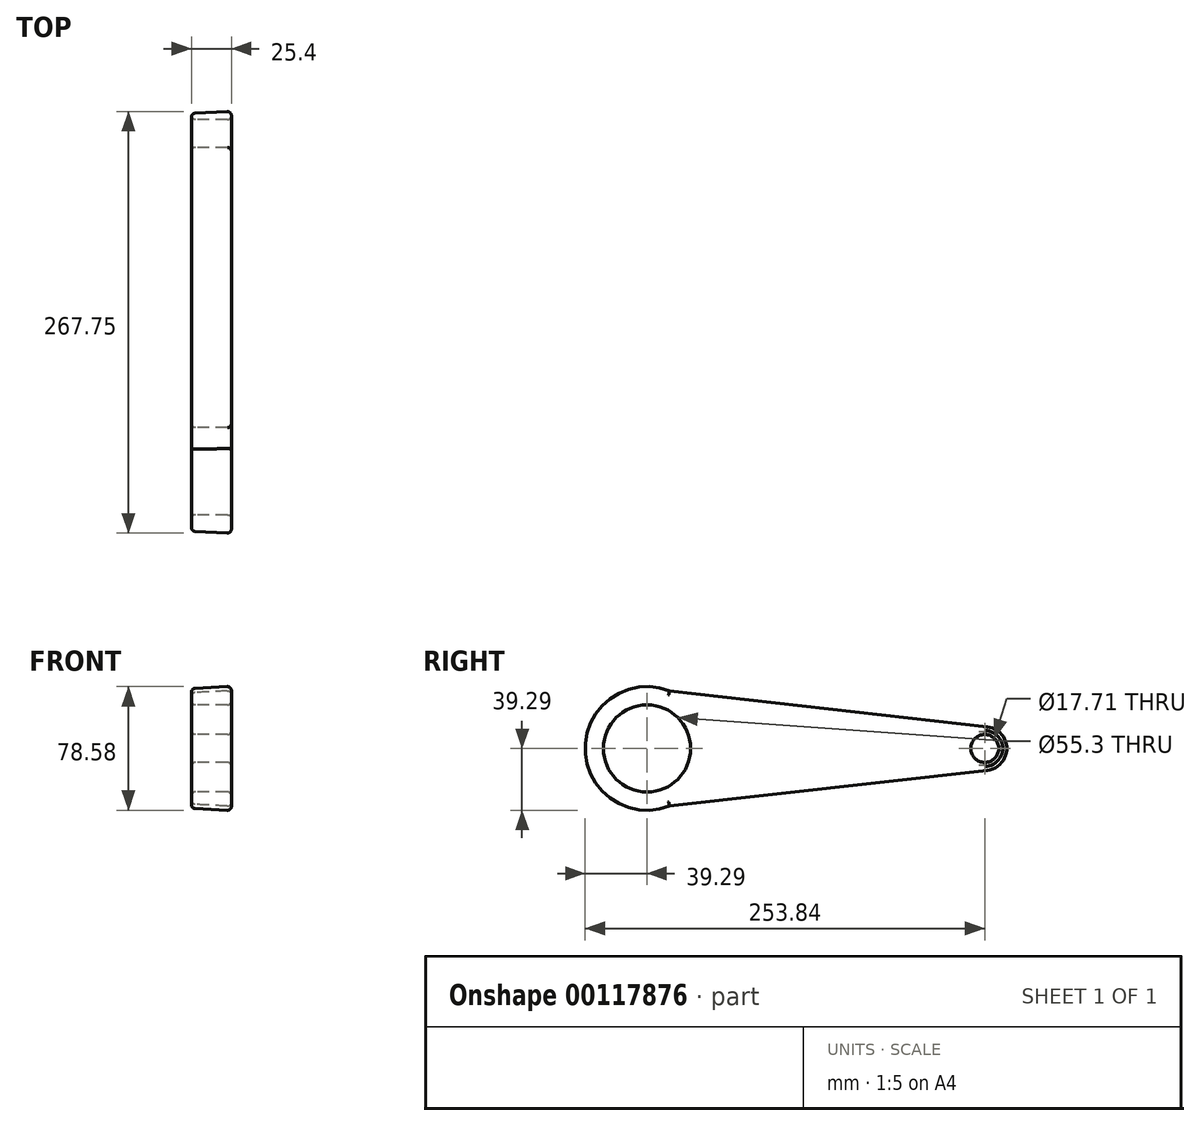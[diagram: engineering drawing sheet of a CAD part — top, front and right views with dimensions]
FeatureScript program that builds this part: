
annotation { "Feature Type Name" : "Feature", "Feature Type Description" : "" }
export const myFeature = defineFeature(function(context is Context, id is Id, definition is map)
    precondition{}
    {
        {
            var Q0;
            Q0=qCreatedBy(makeId("Right.planeOp"),FACE);
            var sketch = newSketch(context, id + "F0", { "sketchPlane" : qUnion([Q0])});
            skCircle(sketch, "E0", {"center": v(0, 0) * mm, "radius": 38.1 * mm});
            skCircle(sketch, "E1", {"center": v(214.57, 0) * mm, "radius": 12.7 * mm});
            skLineSegment(sketch, "E2", {"start": v(14.08, 35.4) * mm, "end": v(216, 12.62) * mm});
            skLineSegment(sketch, "E3", {"start": v(14.08, -35.4) * mm, "end": v(216, -12.62) * mm});
            skSolve(sketch);
        }
        {
            var Q0;
            Q0 = qSketchRegion(id + "F0", true);
            extrude(context, id + "F1", {"entities" : qUnion([Q0]), "depth" : 25.4 * mm, "hasDraft" : true, "draftAngle" : 3 * degree});
        }
        {
            var Q0;
            Q0=qCreatedBy(makeId("Right.planeOp"),FACE);
            var sketch = newSketch(context, id + "F2", { "sketchPlane" : qUnion([Q0])});
            skCircle(sketch, "E4", {"center": v(0, 0) * mm, "radius": 27.65 * mm});
            skCircle(sketch, "E5", {"center": v(214.55, 0) * mm, "radius": 8.85 * mm});
            skSolve(sketch);
        }
        {
            var Q0;
            Q0 = qSketchRegion(id + "F2", true);
            var Q1;
            Q1=makeQuery(id+"F2.imprint","IMPRINT",FACE,{"disambiguationData":[TD([[makeQuery(id+"F2.imprint","IMPRINT",EDGE,{"derivedFrom":sQuery(id+"F2.wireOp",EDGE,"E4")}),1.0]])]});
            extrude(context, id + "F3", {"entities" : qUnion([Q0, Q1]), "operationType" : NewBodyOperationType.REMOVE, "depth" : 118.25 * mm});
        }
        {
            var Q0;
            Q0=makeQuery(id+"F1.opExtrude","CAP_FACE",FACE,{"disambiguationData":[OSD([sQuery(id+"F0.wireOp",EDGE,"E0"),sQuery(id+"F0.wireOp",EDGE,"E1"),sQuery(id+"F0.wireOp",EDGE,"E2"),sQuery(id+"F0.wireOp",EDGE,"E3")])],"isStart":false});
            var Q1;
            Q1=makeQuery(id+"F1.opExtrude","CAP_EDGE",EDGE,{"disambiguationData":[OSD([sQuery(id+"F0.wireOp",EDGE,"E2")])],"isStart":false});
            var Q2;
            Q2=makeQuery(id+"F1.opExtrude","CAP_EDGE",EDGE,{"disambiguationData":[OSD([sQuery(id+"F0.wireOp",EDGE,"E0")])],"isStart":false});
            fillet(context, id + "F4", {"entities" : qUnion([Q0, Q1, Q2]), "radius" : 2.54 * mm, "allowEdgeOverflow" : false});
        }
        {
            var Q0;
            Q0=makeQuery(id+"F1.opExtrude","CAP_FACE",FACE,{"disambiguationData":[OSD([sQuery(id+"F0.wireOp",EDGE,"E0"),sQuery(id+"F0.wireOp",EDGE,"E1"),sQuery(id+"F0.wireOp",EDGE,"E2"),sQuery(id+"F0.wireOp",EDGE,"E3")])],"isStart":true});
            fillet(context, id + "F5", {"entities" : qUnion([Q0]), "radius" : 2.54 * mm, "tangentPropagation" : true, "allowEdgeOverflow" : false});
        }
    });
